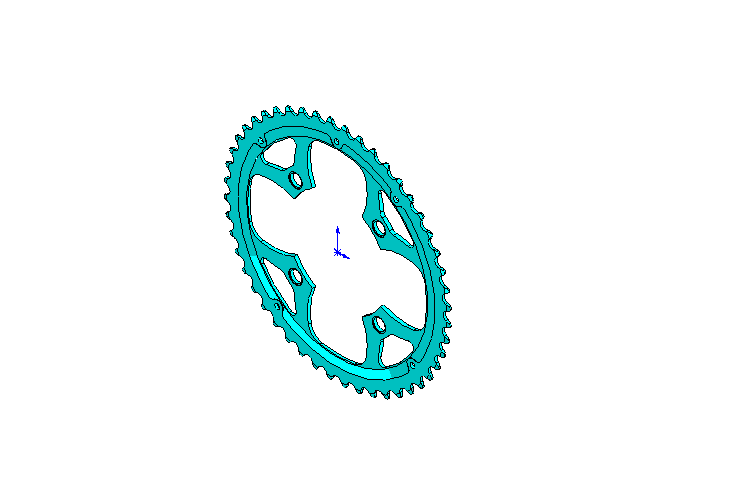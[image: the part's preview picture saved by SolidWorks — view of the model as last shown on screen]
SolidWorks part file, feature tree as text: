
SOLIDWORKS PART (.sldprt)
format: sldprt  version: not decoded by parser v0  size: 2,046,976 bytes
history: native  units: mm
features: sketch x10, cut_extrude x7, plane x4, material x1, revolve x1, cut_revolve x1, pattern_circular x1, extrude x1 (+10 scaffold rows collapsed)
feature tree (36):
  scaffold x10  (default folders/planes/origin — collapsed)
  material  "Matériau <non spécifié>"
  plane  "Plan de face"
  plane  "Plan de dessus"
  plane  "Plan de droite"
  sketch  "Esquisse7"  dims[c1.D1=88.0mm c1.D2=200.0mm c1.D4=2.0mm c1.D5=2.5mm c1.D6=160.0mm c1.D7=~159.105573mm c2.D6=160.0mm c2.D7=174.0mm c2.D8=2.5mm c2.D3=3.0mm]
  revolve  "Révolution1"  Angle=360deg
  plane  "Plan1"
  sketch  "Esquisse4"  dims[D1=3.0mm D2=1.0mm]
  cut_revolve  "Enlèvement de matière-Révolution1"  Angle=360deg
  sketch  "Esquisse2"  dims[c1.D1=8.0mm c1.D3=4.0mm c2.D1=8.0mm c2.D3=4.0mm c2.D4=1.5mm c3.D3=54.75mm c3.D2=9.5mm c4.D3=4.0mm c4.D2=~2.039916mm c5.D2=25.0deg c5.D3=2.0mm]
  cut_extrude  "Enlèv. mat.-Extru.1"  [1 undecoded]
  pattern_circular  "Répétition circulaire1"  Count=48 Angle=7.5deg
  sketch  "Esquisse5"  dims[c1.D1=104.0mm c1.D2=10.0mm c2.D1=104.0mm c2.D3=~32.724562mm c3.D3=90.0deg c3.D4=98.0mm]
  cut_extrude  "Enlèv. mat.-Extru.2"  [1 undecoded]
  sketch  "Esquisse11"  dims[D1=12.0mm]
  cut_extrude  "Enlèv. mat.-Extru.7"  Depth=0.5mm
  sketch  "Esquisse8"  dims[c1.D1=10.0mm c1.D3=3.0mm c1.D5=170.0mm c1.D2=~100.487358mm c2.D2=52.0deg c2.D4=17.0mm c2.D5=~2.330388mm c3.D4=~2.306165mm c4.D4=52.0deg c4.D6=~113.151437mm c5.D6=90.0deg c5.D2=~89.164549mm c6.D2=38.0deg]
  extrude  "Extrusion1"  [1 undecoded]
  sketch  "Esquisse9"
  cut_extrude  "Enlèv. mat.-Extru.5"  [1 undecoded]
  sketch  "Esquisse6"  dims[c1.D1=170.0mm c1.D2=4.2mm c1.D3=2.2mm c2.D3=52.0deg c2.D4=~100.336912mm c3.D4=90.0deg]
  cut_extrude  "Enlèv. mat.-Extru.4"  [1 undecoded]
  sketch  "Esquisse10"  dims[c1.D1=158.0mm c1.D2=45.0mm c1.D5=13.0mm c1.D3=20.0mm c1.D4=58.0mm c2.D3=53.0mm c2.D6=~115.587261mm c3.D6=45.0deg]
  cut_extrude  "Enlèv. mat.-Extru.6"  Depth=10mm
  sketch  "Esquisse12"  dims[c1.D1=122.0mm c1.D2=158.0mm c1.D3=110.0mm c1.D4=4.0mm c1.D5=7.5mm c1.D6=5.0mm c1.D7=110.0mm c2.D5=33.0mm c2.D7=10.0mm]
  cut_extrude  "Enlèv. mat.-Extru.8"  [1 undecoded]
decode coverage: 14 of 21 modeling features carry decoded parameters
note: ~ marks probable driven/reference dimensions
note: 6 parameter values undecoded
summary: no parameter record found for 6 features
note: suppression state not decoded; provenance and decode notes live in map.json
